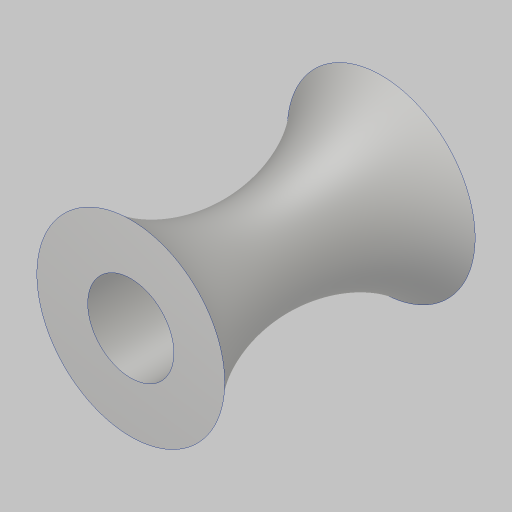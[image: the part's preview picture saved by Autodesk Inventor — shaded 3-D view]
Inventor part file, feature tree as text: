
AUTODESK INVENTOR PART (.ipt)
format: ipt  version: 2023.5 (Build 275446000, 446)  size: 164,864 bytes
history: native  units: in
note: dims shown in document units (in); Inventor stores cm internally (conversion verified against a paired STEP export)
features: sketch x2, revolve x1, extrude x1
ambient origin geometry x8: Origin, YZ Plane, XZ Plane, XY Plane, X Axis, Y Axis, Z Axis, Center Point
bodies: Solid1 (feature_tree)
feature tree (4):
  revolve  "Revolution1"  [1 undecoded]
  extrude  "Extrusion1"  TaperAngle=90.0deg  [1 undecoded]
  sketch  "Sketch1"  dims[d0=2.0in d1=0.75in]
  sketch  "Sketch2"  dims[d2=1.5in d3=90.0deg d4=0.688in d5=0.32in d6=0.0in]
note: 2 required parameter values undecoded (feature->parameter linkage not recoverable at this tier; creation-order binding heuristic only, values carry confidence <= 0.55)